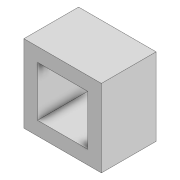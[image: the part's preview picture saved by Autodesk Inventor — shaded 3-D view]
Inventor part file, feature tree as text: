
AUTODESK INVENTOR PART (.ipt)
format: ipt  version: 2020 (Build 240168000, 168)  size: 84,480 bytes
history: native  units: mm
features: extrude x1, sketch x1
ambient origin geometry x8: Origin, YZ Plane, XZ Plane, XY Plane, X Axis, Y Axis, Z Axis, Center Point
bodies: Solid1 (feature_tree)
feature tree (2):
  extrude  "Extrusion1"  Depth=5.5mm
  sketch  "Sketch1"  dims[d0=5.5mm d1=5.5mm d2=8.5mm d3=8.5mm d4=6.0mm d5=0.0mm]
